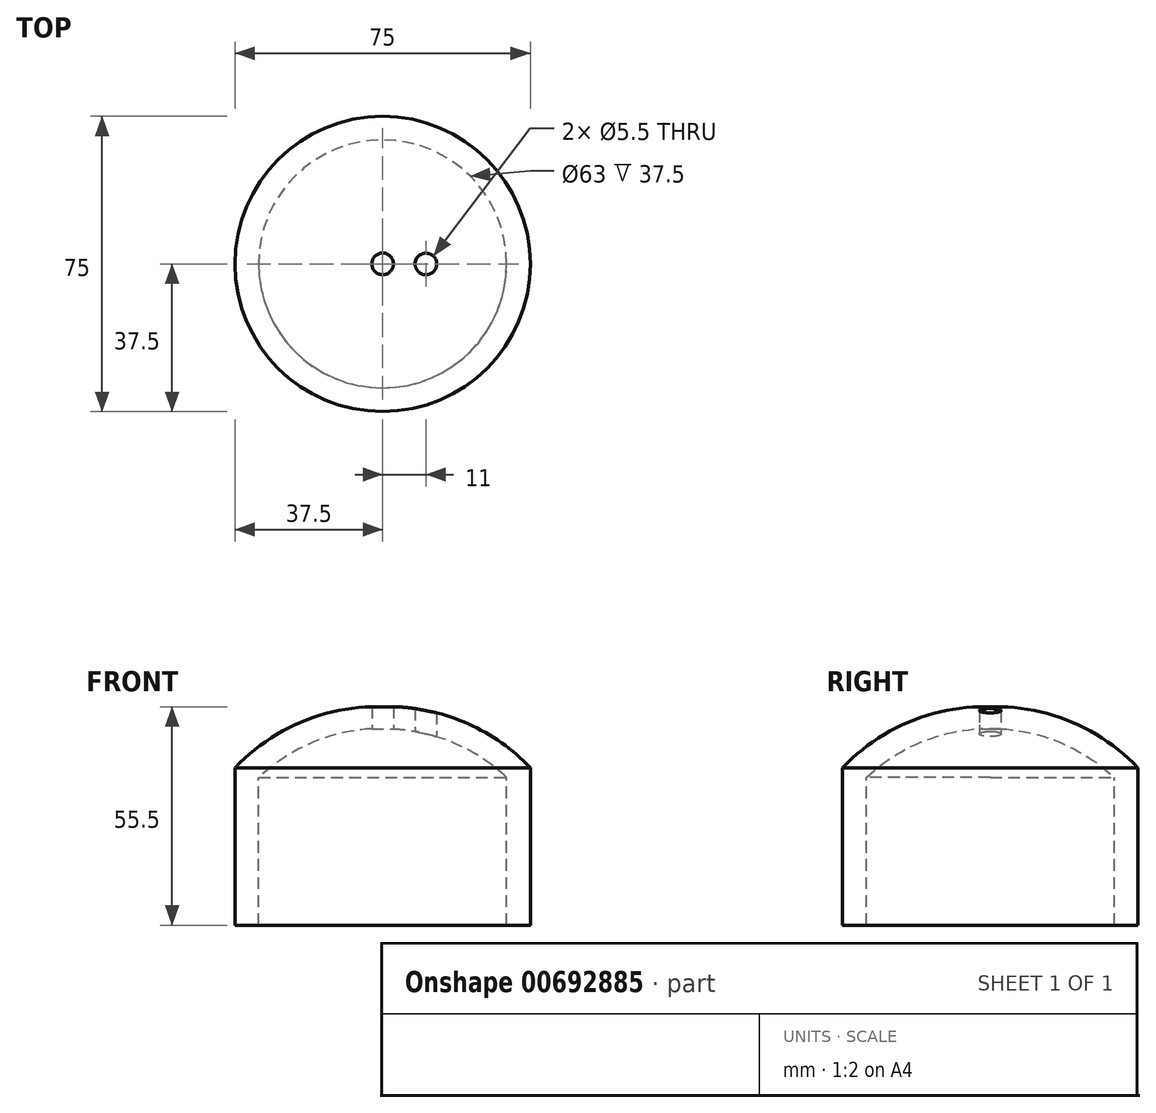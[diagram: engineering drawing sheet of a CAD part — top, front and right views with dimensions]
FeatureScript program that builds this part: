
annotation { "Feature Type Name" : "Feature", "Feature Type Description" : "" }
export const myFeature = defineFeature(function(context is Context, id is Id, definition is map)
    precondition{}
    {
        {
            var Q0;
            Q0=qCreatedBy(makeId("Front.planeOp"),FACE);
            var sketch = newSketch(context, id + "F0", { "sketchPlane" : qUnion([Q0])});
            skLineSegment(sketch, "E0", {"start": v(-37.5, 0) * mm, "end": v(-37.5, 40) * mm});
            skLineSegment(sketch, "E1", {"start": v(-37.5, 40) * mm, "end": v(-37.5, 0) * mm});
            skPoint(sketch, "E2", {"position": v(0, 55.5) * mm});
            skArc(sketch, "E3", {"start": v(0, 55.5) * mm, "mid": v(-20.4, 51.73) * mm, "end": v(-37.5, 40) * mm});
            skLineSegment(sketch, "E4", {"start": v(-37.5, 0) * mm, "end": v(-31.5, 0) * mm});
            skLineSegment(sketch, "E5", {"start": v(-31.5, 0) * mm, "end": v(-31.5, 37.5) * mm});
            skPoint(sketch, "E6", {"position": v(0, 50) * mm});
            skArc(sketch, "E7", {"start": v(0, 50) * mm, "mid": v(-16.94, 46.76) * mm, "end": v(-31.5, 37.5) * mm});
            skLineSegment(sketch, "E8", {"start": v(0, 50) * mm, "end": v(0, 55.5) * mm});
            skLineSegment(sketch, "E9", {"start": v(0, 0) * mm, "end": v(0, -29.82) * mm});
            skSolve(sketch);
        }
        {
            var Q0;
            Q0 = qSketchRegion(id + "F0", true);
            var Q1;
            Q1=sQuery(id+"F0.wireOp",EDGE,"E9");
            revolve(context, id + "F1", {"entities" : qUnion([Q0]), "axis" : qUnion([Q1]), "revolveType" : RevolveType.FULL});
        }
        {
            var Q0;
            Q0=qCreatedBy(makeId("Top.planeOp"),FACE);
            var sketch = newSketch(context, id + "F2", { "sketchPlane" : qUnion([Q0])});
            skCircle(sketch, "E10", {"center": v(0, 0) * mm, "radius": 2.75 * mm});
            skSolve(sketch);
        }
        {
            var Q0;
            Q0 = qSketchRegion(id + "F2", true);
            extrude(context, id + "F3", {"entities" : qUnion([Q0]), "operationType" : NewBodyOperationType.REMOVE, "depth" : 60 * mm, "offsetDistance" : 25 * mm});
        }
        {
            var Q0;
            Q0=qCreatedBy(makeId("Top.planeOp"),FACE);
            var sketch = newSketch(context, id + "F4", { "sketchPlane" : qUnion([Q0])});
            skCircle(sketch, "E11", {"center": v(11, 0) * mm, "radius": 2.75 * mm});
            skSolve(sketch);
        }
        {
            var Q0;
            Q0 = qSketchRegion(id + "F4", true);
            extrude(context, id + "F5", {"entities" : qUnion([Q0]), "operationType" : NewBodyOperationType.REMOVE, "depth" : 60 * mm, "offsetDistance" : 25 * mm});
        }
    });
